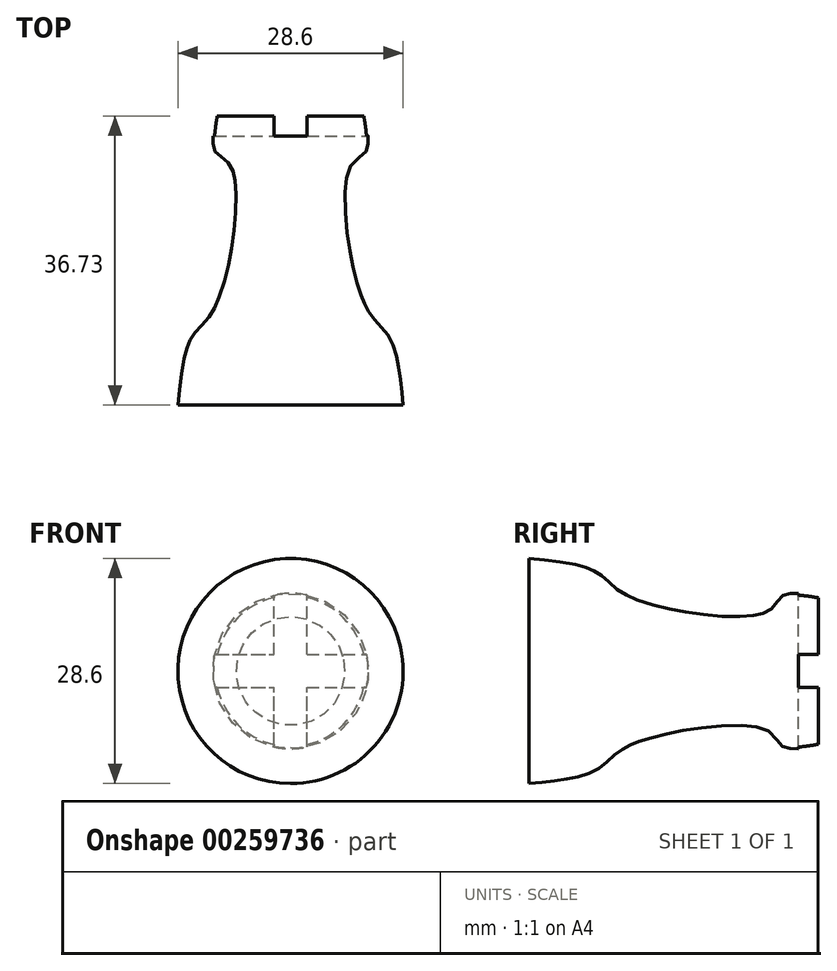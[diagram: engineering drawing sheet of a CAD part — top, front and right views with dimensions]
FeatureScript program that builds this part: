
annotation { "Feature Type Name" : "Feature", "Feature Type Description" : "" }
export const myFeature = defineFeature(function(context is Context, id is Id, definition is map)
    precondition{}
    {
        {
            var Q0;
            Q0=qCreatedBy(makeId("Top.planeOp"),FACE);
            var sketch = newSketch(context, id + "F0", { "sketchPlane" : qUnion([Q0])});
            skLineSegment(sketch, "E0", {"start": v(0, 0) * mm, "end": v(0, 36.73) * mm});
            skLineSegment(sketch, "E1", {"start": v(0, 36.73) * mm, "end": v(9.54, 36.73) * mm});
            skFitSpline(sketch, "E2", {"points": [v(9.54, 36.73) * mm, v(9.54, 32.16) * mm, v(7.45, 30.07) * mm, v(9.54, 12.56) * mm, v(12.59, 8.56) * mm, v(14.3, 0) * mm], "startDerivative": vector(5.5, -34.25) * mm, "endDerivative": vector(4.51, -45.56) * mm});
            skLineSegment(sketch, "E3", {"start": v(0, 0) * mm, "end": v(14.3, 0) * mm});
            skSolve(sketch);
        }
        {
            var Q0;
            Q0 = qSketchRegion(id + "F0", true);
            var Q1;
            Q1=sQuery(id+"F0.wireOp",EDGE,"E0");
            revolve(context, id + "F1", {"entities" : qUnion([Q0]), "axis" : qUnion([Q1]), "revolveType" : RevolveType.FULL});
        }
        {
            var Q0;
            Q0=makeQuery(id+"F1.opRevolve","SWEPT_FACE",FACE,{"disambiguationData":[OSD([sQuery(id+"F0.wireOp",EDGE,"E1")])]});
            var sketch = newSketch(context, id + "F2", { "sketchPlane" : qUnion([Q0])});
            skLineSegment(sketch, "E4.bottom", {"start": v(2.1, -22.12) * mm, "end": v(-2.1, -22.12) * mm});
            skLineSegment(sketch, "E4.top", {"start": v(2.1, 22.12) * mm, "end": v(-2.1, 22.12) * mm});
            skLineSegment(sketch, "E4.left", {"start": v(2.1, -22.12) * mm, "end": v(2.1, 22.12) * mm});
            skLineSegment(sketch, "E4.right", {"start": v(-2.1, -22.12) * mm, "end": v(-2.1, 22.12) * mm});
            skPoint(sketch, "E4.middle", {"position": v(0, 0) * mm});
            skLineSegment(sketch, "E5.bottom", {"start": v(19.74, -2.1) * mm, "end": v(-19.74, -2.1) * mm});
            skLineSegment(sketch, "E5.top", {"start": v(19.74, 2.1) * mm, "end": v(-19.74, 2.1) * mm});
            skLineSegment(sketch, "E5.left", {"start": v(19.74, -2.1) * mm, "end": v(19.74, 2.1) * mm});
            skLineSegment(sketch, "E5.right", {"start": v(-19.74, -2.1) * mm, "end": v(-19.74, 2.1) * mm});
            skSolve(sketch);
        }
        {
            var Q0;
            Q0 = qSketchRegion(id + "F2", true);
            extrude(context, id + "F3", {"entities" : qUnion([Q0]), "operationType" : NewBodyOperationType.REMOVE, "oppositeDirection" : true, "depth" : 2.54 * mm});
        }
    });
